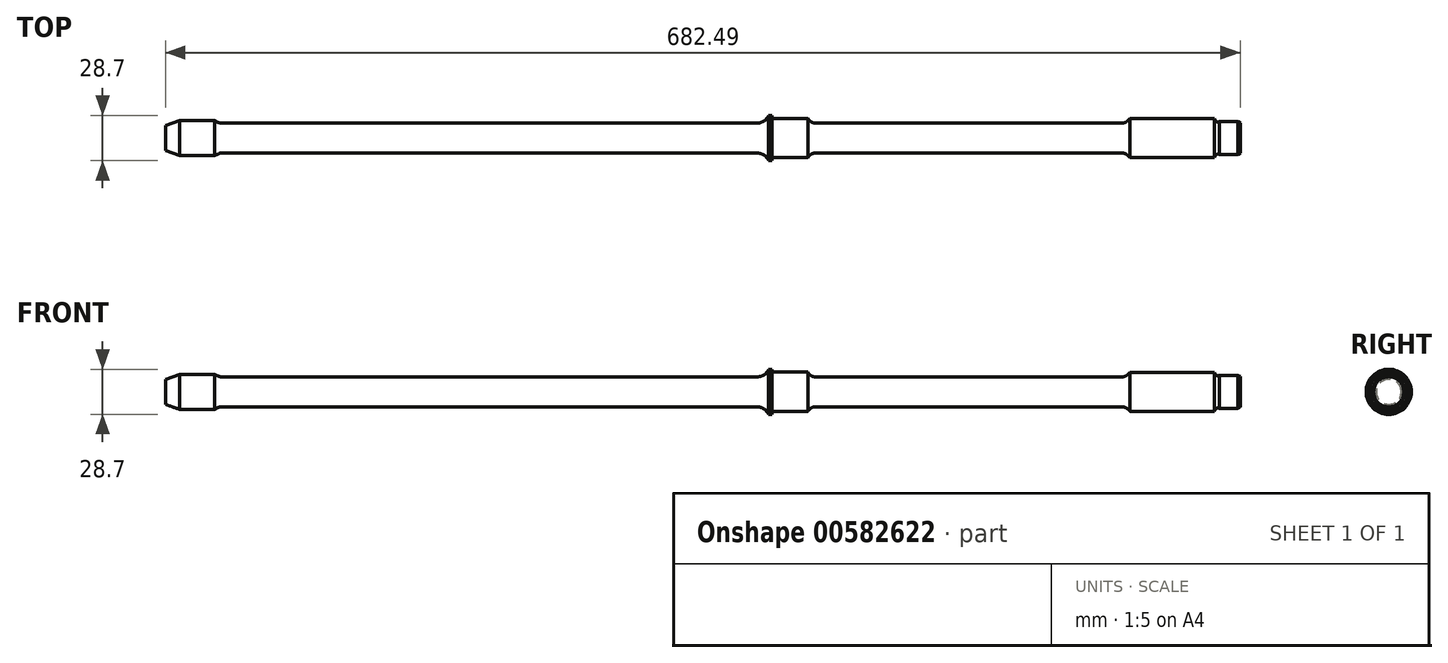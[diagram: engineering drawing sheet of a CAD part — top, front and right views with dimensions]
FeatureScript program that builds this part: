
annotation { "Feature Type Name" : "Feature", "Feature Type Description" : "" }
export const myFeature = defineFeature(function(context is Context, id is Id, definition is map)
    precondition{}
    {
        {
            var Q0;
            Q0=qCreatedBy(makeId("Front.planeOp"),FACE);
            var sketch = newSketch(context, id + "F0", { "sketchPlane" : qUnion([Q0])});
            skLineSegment(sketch, "E0", {"start": v(-350.6, 9.53) * mm, "end": v(-2, 9.53) * mm});
            skLineSegment(sketch, "E1", {"start": v(-2, 9.53) * mm, "end": v(-2, 14.35) * mm});
            skLineSegment(sketch, "E2", {"start": v(-2, 14.35) * mm, "end": v(0, 14.35) * mm});
            skLineSegment(sketch, "E3", {"start": v(0, 14.35) * mm, "end": v(0, 12.5) * mm});
            skLineSegment(sketch, "E4", {"start": v(23, 9.52) * mm, "end": v(224.58, 9.52) * mm});
            skLineSegment(sketch, "E5", {"start": v(224.58, 9.52) * mm, "end": v(227.5, 12.45) * mm});
            skLineSegment(sketch, "E6", {"start": v(227.5, 12.45) * mm, "end": v(280.97, 12.45) * mm});
            skLineSegment(sketch, "E7", {"start": v(280.97, 12.45) * mm, "end": v(281.73, 11.13) * mm});
            skLineSegment(sketch, "E8", {"start": v(284.18, 10.49) * mm, "end": v(296, 10.49) * mm});
            skLineSegment(sketch, "E9", {"start": v(296, 10.49) * mm, "end": v(297.5, 9.62) * mm});
            skLineSegment(sketch, "E10", {"start": v(297.5, 9.62) * mm, "end": v(297.5, 0) * mm});
            skLineSegment(sketch, "E11", {"start": v(297.5, 0) * mm, "end": v(-385, 0) * mm});
            skLineSegment(sketch, "E12", {"start": v(-385, 0) * mm, "end": v(-385, 8) * mm});
            skLineSegment(sketch, "E13", {"start": v(-385, 8) * mm, "end": v(-376.25, 11.11) * mm});
            skLineSegment(sketch, "E14", {"start": v(-376.25, 11.11) * mm, "end": v(-354, 11.11) * mm});
            skLineSegment(sketch, "E15", {"start": v(-354, 11.11) * mm, "end": v(-350.6, 9.53) * mm});
            skArc(sketch, "E16", {"start": v(281.73, 11.13) * mm, "mid": v(282.82, 10.3) * mm, "end": v(284.18, 10.49) * mm});
            skLineSegment(sketch, "E17", {"start": v(0, 12.5) * mm, "end": v(23, 12.5) * mm});
            skLineSegment(sketch, "E18", {"start": v(23, 12.5) * mm, "end": v(23, 9.52) * mm});
            skSolve(sketch);
        }
        {
            var Q0;
            Q0=makeQuery(id+"F0.imprint","IMPRINT",FACE,{"disambiguationData":[TD([[makeQuery(id+"F0.imprint","IMPRINT",EDGE,{"derivedFrom":sQuery(id+"F0.wireOp",EDGE,"E0")}),-1.0]])]});
            var Q1;
            Q1=sQuery(id+"F0.wireOp",EDGE,"E11");
            revolve(context, id + "F1", {"entities" : qUnion([Q0]), "axis" : qUnion([Q1]), "revolveType" : RevolveType.FULL});
        }
        {
            var Q0;
            Q0=makeQuery(id+"F1.opRevolve","SWEPT_EDGE",EDGE,{"disambiguationData":[OSD([sQuery(id+"F0.wireOp",EDGE,"E0"),sQuery(id+"F0.wireOp",EDGE,"E1")])]});
            fillet(context, id + "F2", {"entities" : qUnion([Q0]), "radius" : 8 * mm, "tangentPropagation" : true, "allowEdgeOverflow" : false});
        }
        {
            var Q0;
            Q0=makeQuery(id+"F1.opRevolve","SWEPT_EDGE",EDGE,{"disambiguationData":[OSD([sQuery(id+"F0.wireOp",EDGE,"E4"),sQuery(id+"F0.wireOp",EDGE,"E18")])]});
            fillet(context, id + "F3", {"entities" : qUnion([Q0]), "radius" : 5 * mm, "tangentPropagation" : true, "allowEdgeOverflow" : false});
        }
        {
            var Q0;
            Q0=makeQuery(id+"F1.opRevolve","SWEPT_EDGE",EDGE,{"disambiguationData":[OSD([sQuery(id+"F0.wireOp",EDGE,"E3"),sQuery(id+"F0.wireOp",EDGE,"E17")])]});
            fillet(context, id + "F4", {"entities" : qUnion([Q0]), "radius" : 0.25 * mm, "tangentPropagation" : true, "allowEdgeOverflow" : false});
        }
        {
            var Q0;
            Q0=makeQuery(id+"F1.opRevolve","SWEPT_EDGE",EDGE,{"disambiguationData":[OSD([sQuery(id+"F0.wireOp",EDGE,"E0"),sQuery(id+"F0.wireOp",EDGE,"E15")])]});
            fillet(context, id + "F5", {"entities" : qUnion([Q0]), "radius" : 5 * mm, "tangentPropagation" : true, "allowEdgeOverflow" : false});
        }
        {
            var Q0;
            Q0=makeQuery(id+"F1.opRevolve","SWEPT_EDGE",EDGE,{"disambiguationData":[OSD([sQuery(id+"F0.wireOp",EDGE,"E4"),sQuery(id+"F0.wireOp",EDGE,"E5")])]});
            fillet(context, id + "F6", {"entities" : qUnion([Q0]), "radius" : 5 * mm, "tangentPropagation" : true, "allowEdgeOverflow" : false});
        }
    });
